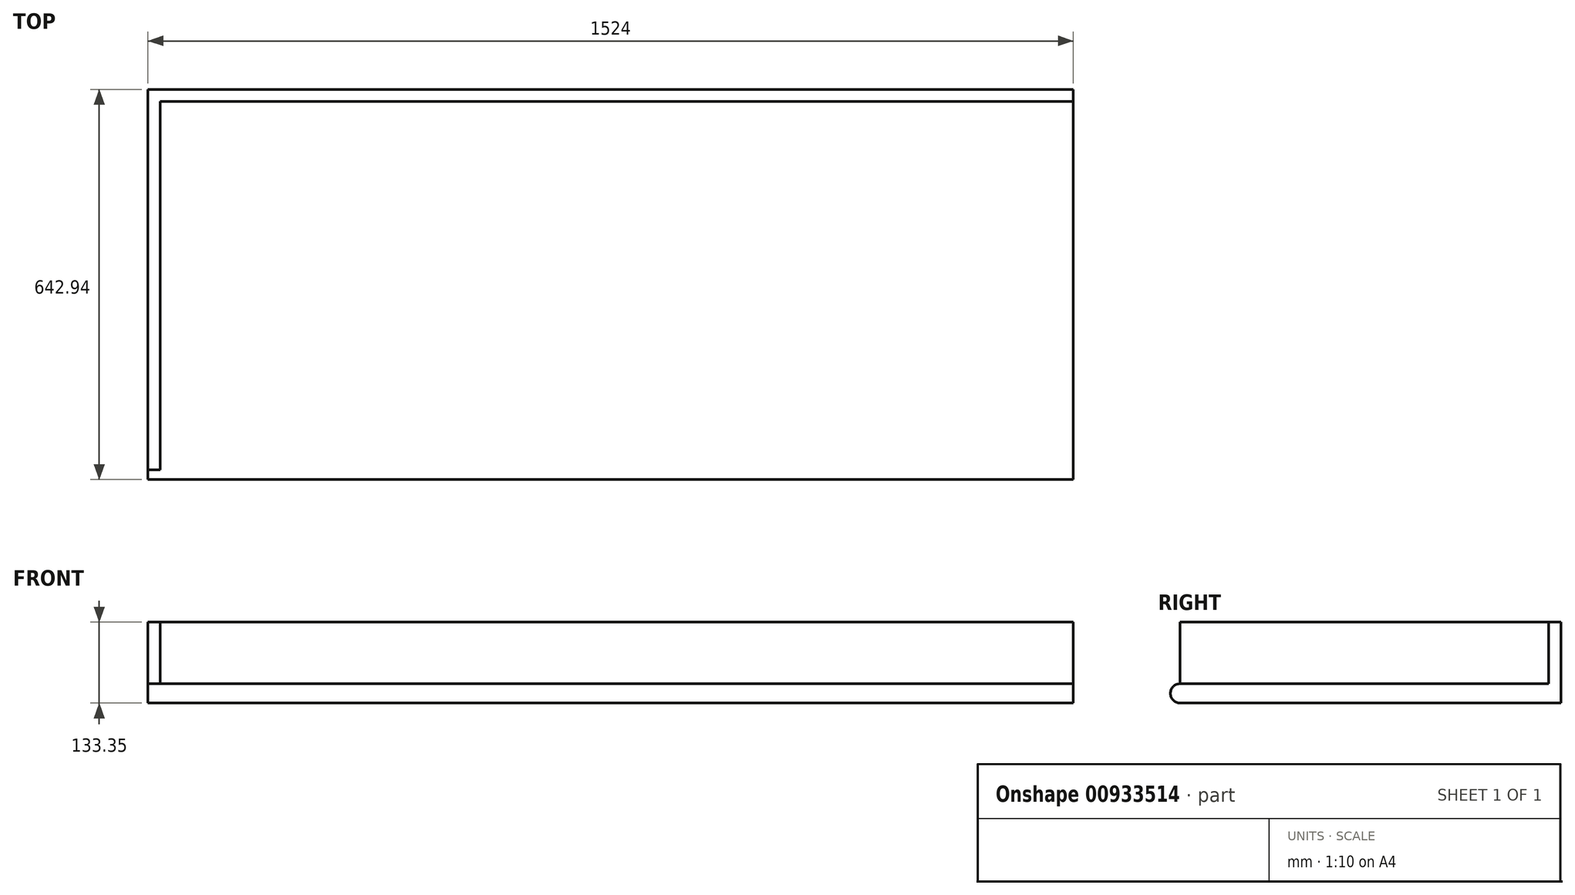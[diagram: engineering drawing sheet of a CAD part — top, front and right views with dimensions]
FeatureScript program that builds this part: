
annotation { "Feature Type Name" : "Feature", "Feature Type Description" : "" }
export const myFeature = defineFeature(function(context is Context, id is Id, definition is map)
    precondition{}
    {
        {
            var Q0;
            Q0=qCreatedBy(makeId("Right.planeOp"),FACE);
            var sketch = newSketch(context, id + "F0", { "sketchPlane" : qUnion([Q0])});
            skLineSegment(sketch, "E0", {"start": v(0, 0) * mm, "end": v(0, 31.75) * mm});
            skLineSegment(sketch, "E1", {"start": v(0, 31.75) * mm, "end": v(-627.06, 31.75) * mm});
            skLineSegment(sketch, "E2", {"start": v(0, 0) * mm, "end": v(-627.06, 0) * mm});
            skArc(sketch, "E3", {"start": v(-627.06, 31.75) * mm, "mid": v(-642.94, 15.87) * mm, "end": v(-627.06, 0) * mm});
            skSolve(sketch);
        }
        {
            var Q0;
            Q0 = qSketchRegion(id + "F0", true);
            extrude(context, id + "F1", {"entities" : qUnion([Q0]), "depth" : 1524 * mm, "offsetDistance" : 25.4 * mm});
        }
        {
            var Q0;
            Q0=makeQuery(id+"F1.opExtrude","SWEPT_FACE",FACE,{"disambiguationData":[OSD([sQuery(id+"F0.wireOp",EDGE,"E1")])]});
            var sketch = newSketch(context, id + "F2", { "sketchPlane" : qUnion([Q0])});
            skLineSegment(sketch, "E4.0", {"start": v(19.99, -19.99) * mm, "end": v(19.99, -627.06) * mm});
            skLineSegment(sketch, "E4.1", {"start": v(1524, -19.99) * mm, "end": v(19.99, -19.99) * mm});
            skLineSegment(sketch, "E5", {"start": v(19.99, -627.06) * mm, "end": v(0, -627.06) * mm});
            skLineSegment(sketch, "E6", {"start": v(1524, -19.99) * mm, "end": v(1524, 0) * mm});
            skLineSegment(sketch, "E7.0", {"start": v(0, 0) * mm, "end": v(0, -627.06) * mm});
            skLineSegment(sketch, "E7.1", {"start": v(1524, 0) * mm, "end": v(0, 0) * mm});
            skSolve(sketch);
        }
        {
            var Q0;
            Q0 = qSketchRegion(id + "F2", true);
            extrude(context, id + "F3", {"entities" : qUnion([Q0]), "operationType" : NewBodyOperationType.ADD, "depth" : 101.6 * mm, "offsetDistance" : 25.4 * mm});
        }
    });
